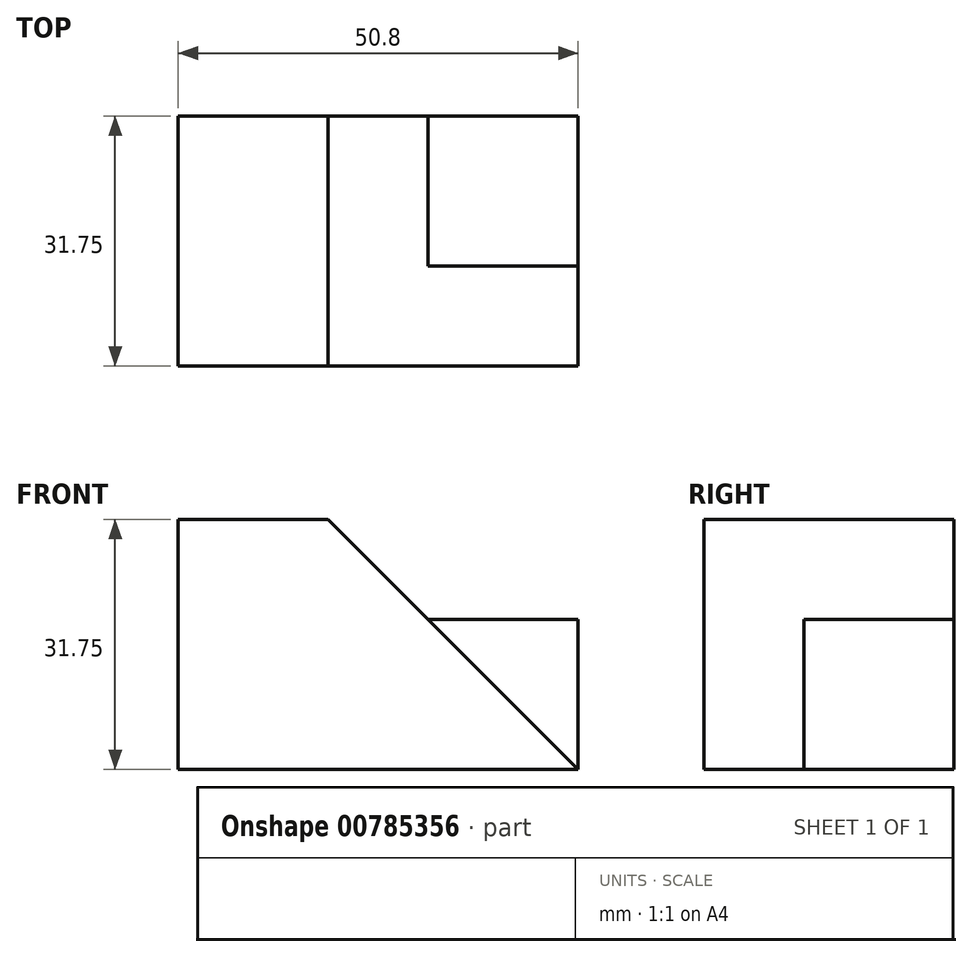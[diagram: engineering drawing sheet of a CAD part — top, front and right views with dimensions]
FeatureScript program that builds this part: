
annotation { "Feature Type Name" : "Feature", "Feature Type Description" : "" }
export const myFeature = defineFeature(function(context is Context, id is Id, definition is map)
    precondition{}
    {
        {
            var Q0;
            Q0=qCreatedBy(makeId("Front.planeOp"),FACE);
            var sketch = newSketch(context, id + "F0", { "sketchPlane" : qUnion([Q0])});
            skLineSegment(sketch, "E0", {"start": v(0, 0) * mm, "end": v(50.8, 0) * mm});
            skLineSegment(sketch, "E1", {"start": v(50.8, 0) * mm, "end": v(50.8, 31.75) * mm});
            skLineSegment(sketch, "E2", {"start": v(50.8, 31.75) * mm, "end": v(0, 31.75) * mm});
            skLineSegment(sketch, "E3", {"start": v(0, 31.75) * mm, "end": v(0, 0) * mm});
            skSolve(sketch);
        }
        {
            var Q0;
            Q0=makeQuery(id+"F0.imprint","IMPRINT",FACE,{"disambiguationData":[TD([[makeQuery(id+"F0.imprint","IMPRINT",EDGE,{"derivedFrom":sQuery(id+"F0.wireOp",EDGE,"E0")}),1.0]])]});
            extrude(context, id + "F1", {"entities" : qUnion([Q0]), "depth" : 31.75 * mm, "offsetDistance" : 25.4 * mm});
        }
        {
            var Q0;
            Q0=makeQuery(id+"F1.opExtrude","CAP_FACE",FACE,{"disambiguationData":[OSD([sQuery(id+"F0.wireOp",EDGE,"E0"),sQuery(id+"F0.wireOp",EDGE,"E1"),sQuery(id+"F0.wireOp",EDGE,"E2"),sQuery(id+"F0.wireOp",EDGE,"E3")])],"isStart":true});
            var sketch = newSketch(context, id + "F2", { "sketchPlane" : qUnion([Q0])});
            skLineSegment(sketch, "E4", {"start": v(-50.8, 31.75) * mm, "end": v(-19.05, 31.75) * mm});
            skLineSegment(sketch, "E5", {"start": v(-50.8, 31.75) * mm, "end": v(-50.8, 19.05) * mm});
            skLineSegment(sketch, "E6", {"start": v(-19.05, 31.75) * mm, "end": v(-50.8, 19.05) * mm});
            skSolve(sketch);
        }
        {
            var Q0;
            Q0=makeQuery(id+"F2.imprint","IMPRINT",FACE,{"disambiguationData":[TD([[makeQuery(id+"F2.imprint","IMPRINT",EDGE,{"derivedFrom":sQuery(id+"F2.wireOp",EDGE,"E4")}),-1.0]])]});
            extrude(context, id + "F3", {"entities" : qUnion([Q0]), "operationType" : NewBodyOperationType.REMOVE, "oppositeDirection" : true, "depth" : 76.2 * mm, "offsetDistance" : 25.4 * mm});
        }
        {
            var Q0;
            Q0=makeQuery(id+"F1.opExtrude","CAP_FACE",FACE,{"disambiguationData":[OSD([sQuery(id+"F0.wireOp",EDGE,"E0"),sQuery(id+"F0.wireOp",EDGE,"E1"),sQuery(id+"F0.wireOp",EDGE,"E2"),sQuery(id+"F0.wireOp",EDGE,"E3")])],"isStart":false});
            var sketch = newSketch(context, id + "F4", { "sketchPlane" : qUnion([Q0])});
            skLineSegment(sketch, "E7", {"start": v(50.8, 19.05) * mm, "end": v(31.75, 19.05) * mm});
            skLineSegment(sketch, "E8", {"start": v(31.75, 19.05) * mm, "end": v(50.8, 0) * mm});
            skLineSegment(sketch, "E9", {"start": v(50.8, 0) * mm, "end": v(50.8, 19.05) * mm});
            skSolve(sketch);
        }
        {
            var Q0;
            Q0=makeQuery(id+"F4.imprint","IMPRINT",FACE,{"disambiguationData":[TD([[makeQuery(id+"F4.imprint","IMPRINT",EDGE,{"derivedFrom":sQuery(id+"F4.wireOp",EDGE,"E7")}),1.0]])]});
            extrude(context, id + "F5", {"entities" : qUnion([Q0]), "operationType" : NewBodyOperationType.REMOVE, "oppositeDirection" : true, "depth" : 12.7 * mm, "offsetDistance" : 25.4 * mm});
        }
        {
            var Q0;
            Q0=makeQuery(id+"F1.opExtrude","CAP_FACE",FACE,{"disambiguationData":[OSD([sQuery(id+"F0.wireOp",EDGE,"E0"),sQuery(id+"F0.wireOp",EDGE,"E1"),sQuery(id+"F0.wireOp",EDGE,"E2"),sQuery(id+"F0.wireOp",EDGE,"E3")])],"isStart":false});
            var sketch = newSketch(context, id + "F6", { "sketchPlane" : qUnion([Q0])});
            skLineSegment(sketch, "E10", {"start": v(19.05, 31.75) * mm, "end": v(31.75, 19.05) * mm});
            skLineSegment(sketch, "E11", {"start": v(31.75, 19.05) * mm, "end": v(50.8, 19.05) * mm});
            skLineSegment(sketch, "E12", {"start": v(19.05, 31.75) * mm, "end": v(50.8, 19.05) * mm});
            skSolve(sketch);
        }
        {
            var Q0;
            Q0=makeQuery(id+"F6.imprint","IMPRINT",FACE,{"disambiguationData":[TD([[makeQuery(id+"F6.imprint","IMPRINT",EDGE,{"derivedFrom":sQuery(id+"F6.wireOp",EDGE,"E10")}),1.0]])]});
            extrude(context, id + "F7", {"entities" : qUnion([Q0]), "operationType" : NewBodyOperationType.REMOVE, "oppositeDirection" : true, "depth" : 38.1 * mm, "offsetDistance" : 25.4 * mm});
        }
    });
